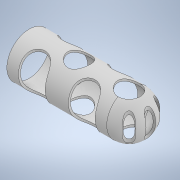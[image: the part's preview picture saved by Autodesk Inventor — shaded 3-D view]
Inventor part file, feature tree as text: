
AUTODESK INVENTOR PART (.ipt)
format: ipt  version: 2020 (Build 240168000, 168)  size: 231,424 bytes
history: native  units: in
note: dims shown in document units (in); Inventor stores cm internally (conversion verified against a paired STEP export)
features: sketch x2, revolve x1, extrude x1
ambient origin geometry x8: Origin, YZ Plane, XZ Plane, XY Plane, X Axis, Y Axis, Z Axis, Center Point
bodies: Solid1 (feature_tree)
feature tree (4):
  revolve  "Revolution1"  [1 undecoded]
  extrude  "Extrusion1"  TaperAngle=90.0deg  [1 undecoded]
  sketch  "Sketch1"  dims[d0=0.9055in d1=2.4803in]
  sketch  "Sketch2"  dims[d2=0.0394in d3=90.0deg d4=0.2362in d5=0.2362in d6=0.2362in d7=0.2362in d8=135.0deg d9=135.0deg d10=0.1969in d11=0.1969in d12=0.1969in d13=2.4803in d14=0.0in d15=0.5in d16=0.0344in]
note: 2 required parameter values undecoded (feature->parameter linkage not recoverable at this tier; creation-order binding heuristic only, values carry confidence <= 0.55)